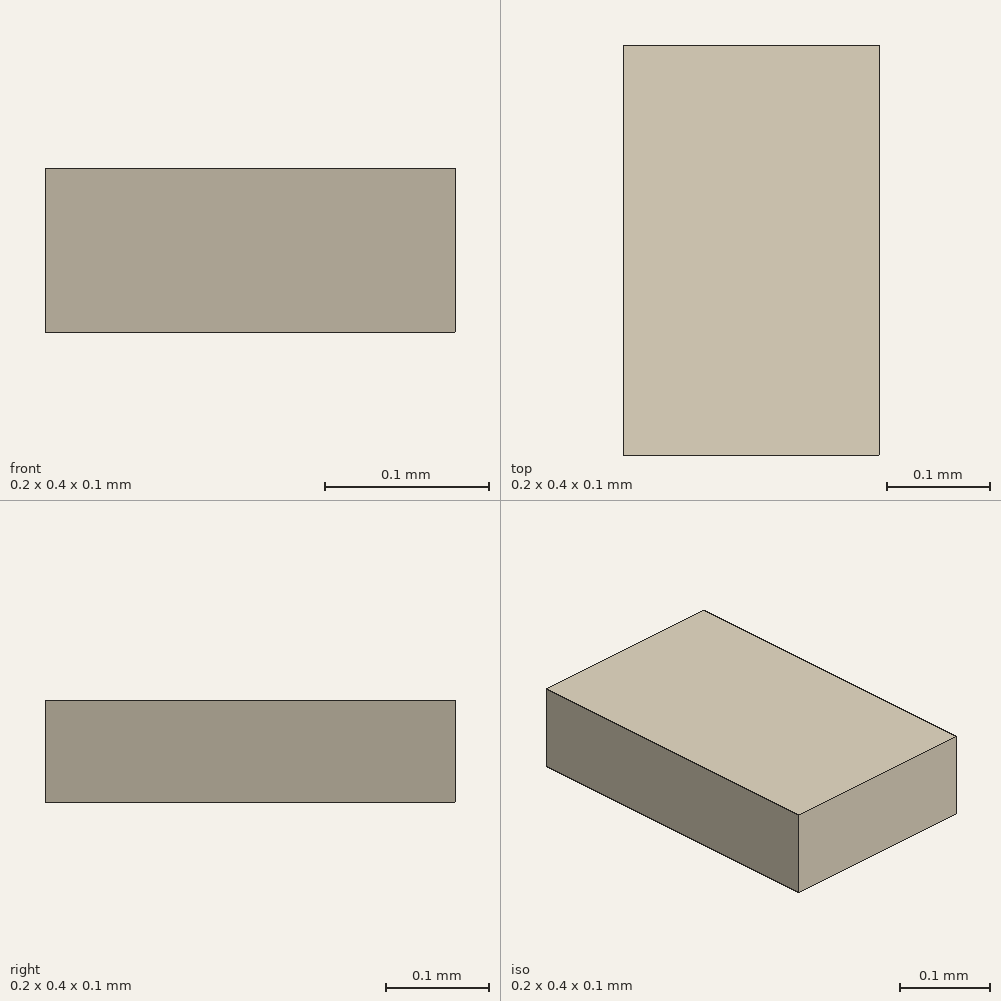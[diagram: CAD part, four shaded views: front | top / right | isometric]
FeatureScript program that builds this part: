
annotation { "Feature Type Name" : "Feature", "Feature Type Description" : "" }
export const myFeature = defineFeature(function(context is Context, id is Id, definition is map)
    precondition{}
    {
        {
            var Q0;
            Q0=qCreatedBy(makeId("Front.planeOp"),FACE);
            var sketch = newSketch(context, id + "F0", { "sketchPlane" : qUnion([Q0])});
            skLineSegment(sketch, "E0.bottom", {"start": v(0.12, 0.05) * mm, "end": v(-0.12, 0.05) * mm});
            skLineSegment(sketch, "E0.top", {"start": v(0.13, -0.05) * mm, "end": v(-0.12, -0.05) * mm});
            skLineSegment(sketch, "E0.left", {"start": v(0.12, 0.05) * mm, "end": v(0.12, -0.05) * mm});
            skLineSegment(sketch, "E0.right", {"start": v(-0.12, 0.05) * mm, "end": v(-0.12, -0.05) * mm});
            skPoint(sketch, "E0.middle", {"position": v(0, 0) * mm});
            skSolve(sketch);
        }
        {
            var Q0;
            Q0 = qSketchRegion(id + "F0", true);
            extrude(context, id + "F1", {"entities" : qUnion([Q0]), "depth" : 0.4 * mm});
        }
    });
